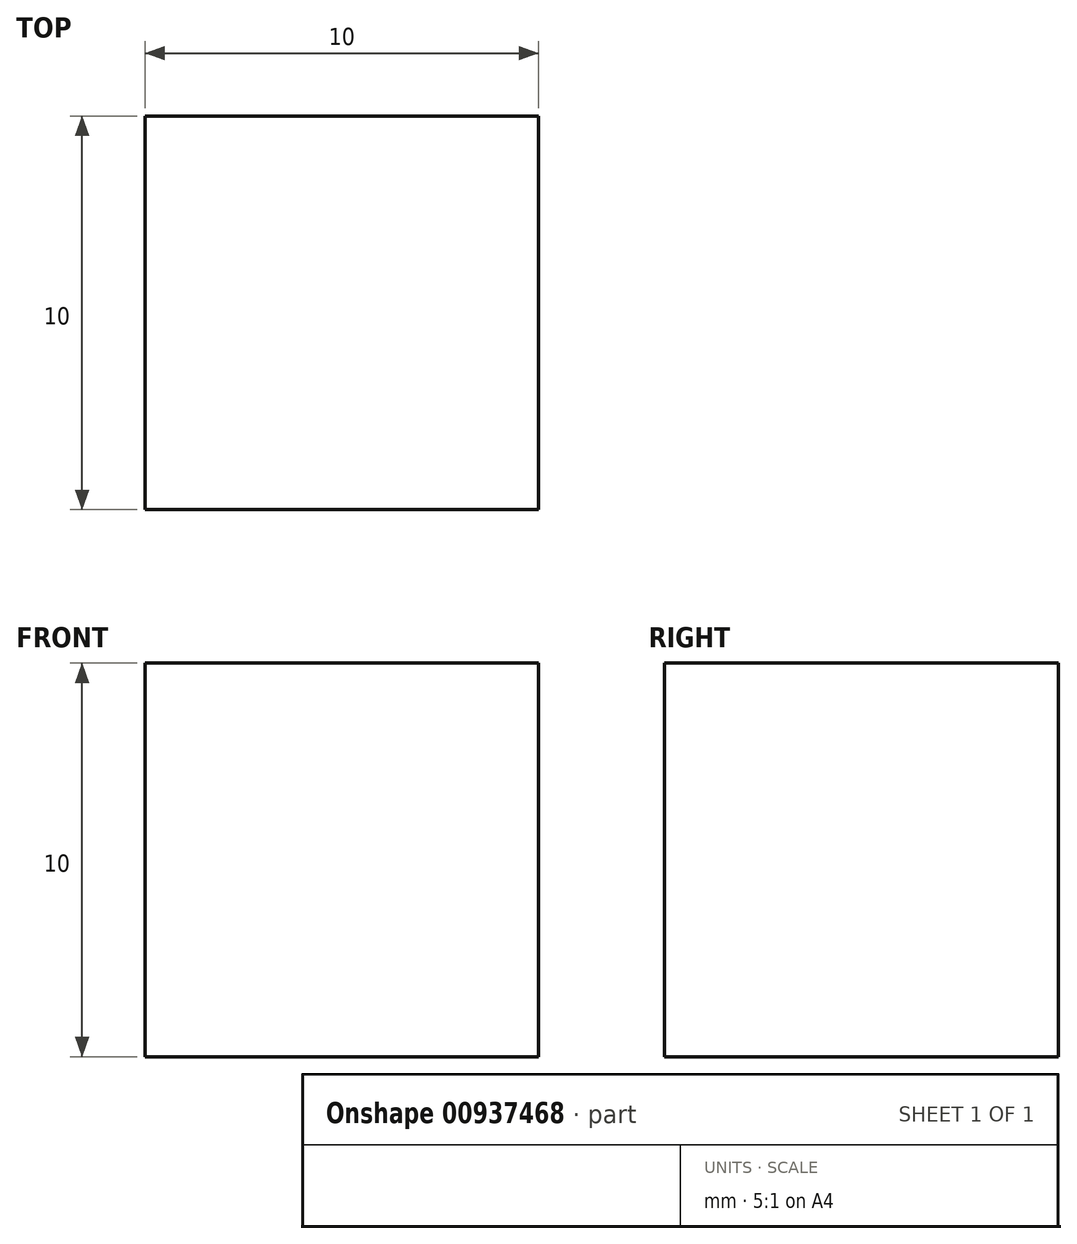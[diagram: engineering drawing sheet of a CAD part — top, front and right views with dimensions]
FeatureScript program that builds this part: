
annotation { "Feature Type Name" : "Feature", "Feature Type Description" : "" }
export const myFeature = defineFeature(function(context is Context, id is Id, definition is map)
    precondition{}
    {
        {
            var Q0;
            Q0=qCreatedBy(makeId("Top.planeOp"),FACE);
            var sketch = newSketch(context, id + "F0", { "sketchPlane" : qUnion([Q0])});
            skLineSegment(sketch, "E0.bottom", {"start": v(0, 0) * mm, "end": v(-10, 0) * mm});
            skLineSegment(sketch, "E0.top", {"start": v(0, 10) * mm, "end": v(-10, 10) * mm});
            skLineSegment(sketch, "E0.left", {"start": v(0, 0) * mm, "end": v(0, 10) * mm});
            skLineSegment(sketch, "E0.right", {"start": v(-10, 0) * mm, "end": v(-10, 10) * mm});
            skSolve(sketch);
        }
        {
            var Q0;
            Q0 = qSketchRegion(id + "F0", true);
            extrude(context, id + "F1", {"entities" : qUnion([Q0]), "depth" : 10 * mm, "offsetDistance" : 25 * mm});
        }
    });
